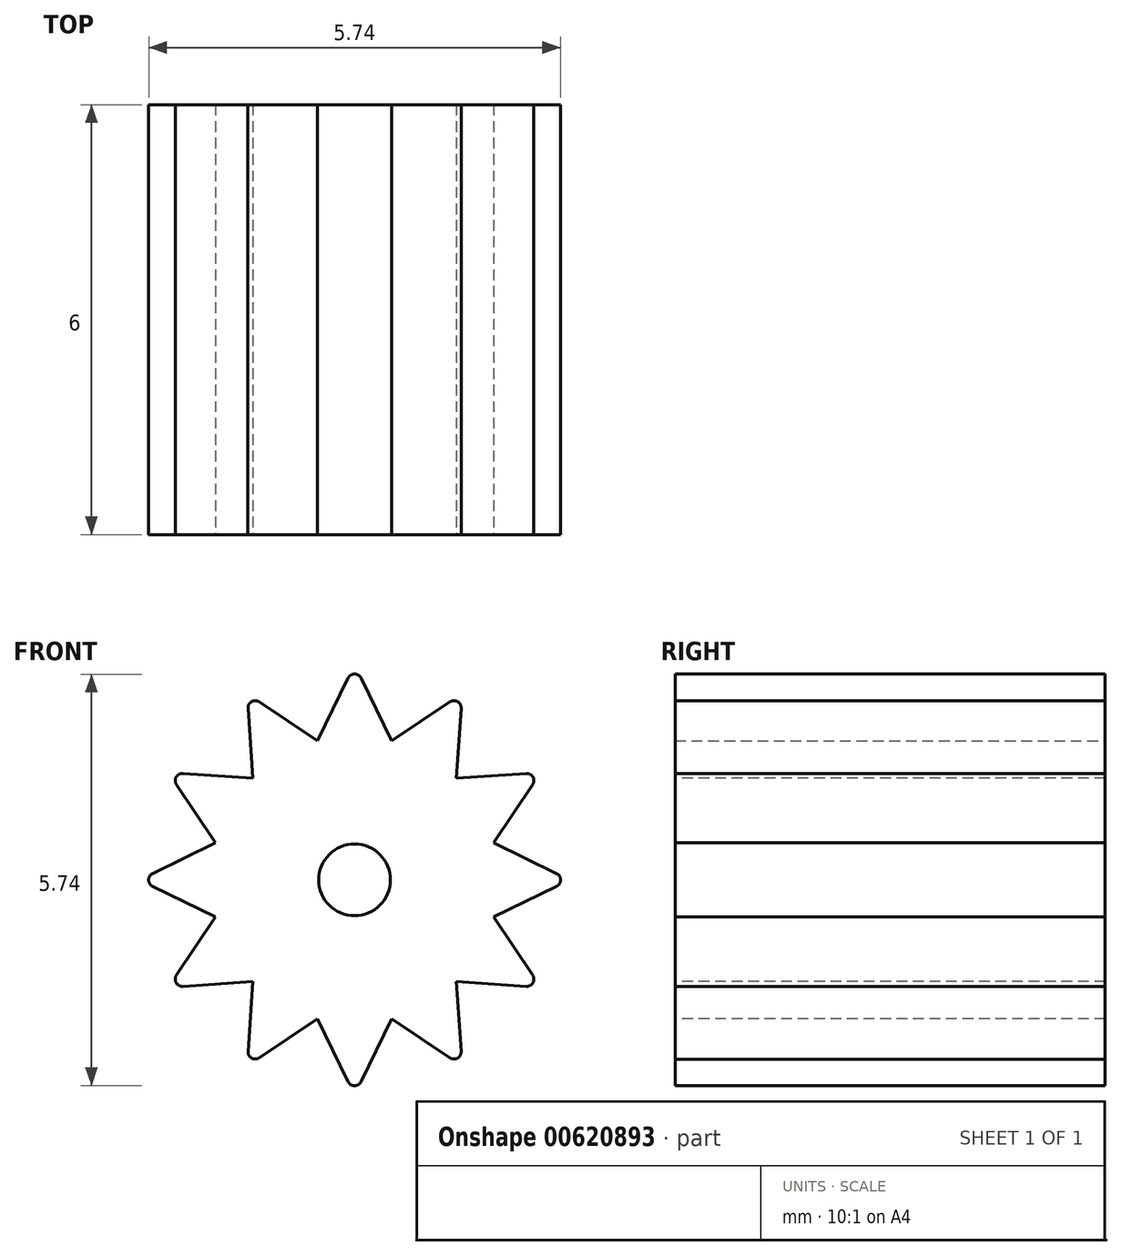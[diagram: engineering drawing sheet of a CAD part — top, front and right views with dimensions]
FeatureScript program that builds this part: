
annotation { "Feature Type Name" : "Feature", "Feature Type Description" : "" }
export const myFeature = defineFeature(function(context is Context, id is Id, definition is map)
    precondition{}
    {
        {
            var Q0;
            Q0=qCreatedBy(makeId("Front.planeOp"),FACE);
            var sketch = newSketch(context, id + "F0", { "sketchPlane" : qUnion([Q0])});
            skCircle(sketch, "E0", {"center": v(0, 0) * mm, "radius": 2 * mm});
            skCircle(sketch, "E1", {"center": v(0, 0) * mm, "radius": 0.5 * mm});
            skLineSegment(sketch, "E2", {"start": v(0, 3) * mm, "end": v(0, 2) * mm, "construction": true});
            skLineSegment(sketch, "E3", {"start": v(0, 3) * mm, "end": v(-0.52, 1.93) * mm});
            skLineSegment(sketch, "E4.MirrorCS", {"start": v(0, 3) * mm, "end": v(0.52, 1.93) * mm});
            skSolve(sketch);
        }
        {
            var Q0;
            Q0=makeQuery(id+"F0.imprint","IMPRINT",FACE,{"disambiguationData":[TD([[makeQuery(id+"F0.imprint","IMPRINT",EDGE,{"derivedFrom":sQuery(id+"F0.wireOp",EDGE,"E1")}),-1.0]])]});
            extrude(context, id + "F1", {"entities" : qUnion([Q0]), "depth" : 6 * mm, "offsetDistance" : 25 * mm});
        }
        {
            var Q0;
            {var subQ0=sQuery(id+"F0.wireOp",EDGE,"E3");Q0=makeQuery(id+"F0.imprint","IMPRINT",FACE,{"disambiguationData":[TD([[makeQuery(id+"F0.imprint","IMPRINT",EDGE,{"derivedFrom":subQ0}),1.0]])]});}
            extrude(context, id + "F2", {"entities" : qUnion([Q0]), "depth" : 6 * mm, "offsetDistance" : 25 * mm});
        }
        {
            var Q0;
            Q0=makeQuery(id+"F2.opExtrude","SWEPT_EDGE",EDGE,{"disambiguationData":[OSD([sQuery(id+"F0.wireOp",EDGE,"E3"),sQuery(id+"F0.wireOp",EDGE,"E4.MirrorCS")])]});
            fillet(context, id + "F3", {"entities" : qUnion([Q0]), "radius" : 0.1 * mm, "tangentPropagation" : true, "allowEdgeOverflow" : false});
        }
        {
            var Q0;
            Q0=makeQuery(id+"F2.opExtrude","SWEPT_BODY",BODY,{"disambiguationData":[OSD([sQuery(id+"F0.wireOp",EDGE,"E0"),sQuery(id+"F0.wireOp",EDGE,"E3"),sQuery(id+"F0.wireOp",EDGE,"E4.MirrorCS")])]});
            var Q1;
            Q1=sQuery(id+"F0.wireOp",EDGE,"E0");
            circularPattern(context, id + "F4", {"operationType" : NewBodyOperationType.ADD, "entities" : qUnion([Q0]), "axis" : qUnion([Q1]), "angle" : 360 * degree, "instanceCount" : 12, "equalSpace" : true});
        }
    });
